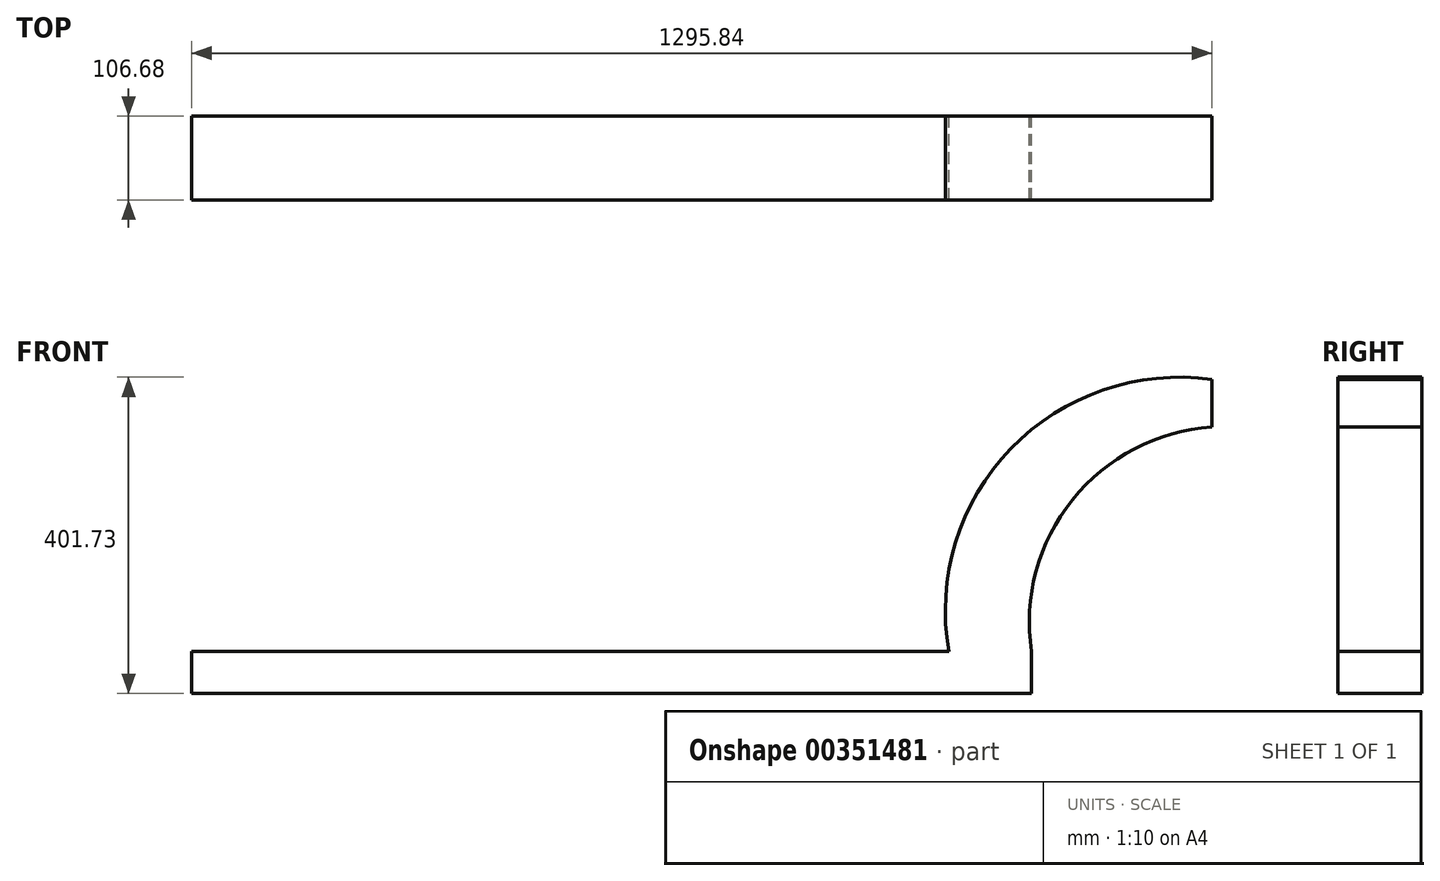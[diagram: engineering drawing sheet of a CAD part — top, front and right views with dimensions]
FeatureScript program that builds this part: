
annotation { "Feature Type Name" : "Feature", "Feature Type Description" : "" }
export const myFeature = defineFeature(function(context is Context, id is Id, definition is map)
    precondition{}
    {
        {
            var Q0;
            Q0=qCreatedBy(makeId("Front.planeOp"),FACE);
            var sketch = newSketch(context, id + "F0", { "sketchPlane" : qUnion([Q0])});
            skLineSegment(sketch, "E0.bottom", {"start": v(-548.92, 0) * mm, "end": v(517.88, 0) * mm});
            skLineSegment(sketch, "E0.top", {"start": v(-548.92, 53.35) * mm, "end": v(412.72, 53.35) * mm});
            skLineSegment(sketch, "E0.left", {"start": v(-548.92, 0) * mm, "end": v(-548.92, 53.35) * mm});
            skLineSegment(sketch, "E0.right", {"start": v(517.88, 0) * mm, "end": v(517.88, 53.35) * mm});
            skArc(sketch, "E1", {"start": v(746.92, 338.17) * mm, "mid": v(569.88, 246.04) * mm, "end": v(517.88, 53.35) * mm});
            skLineSegment(sketch, "E2", {"start": v(746.92, 338.17) * mm, "end": v(746.92, 398.87) * mm});
            skArc(sketch, "E3", {"start": v(746.92, 398.87) * mm, "mid": v(491.96, 311.1) * mm, "end": v(412.72, 53.35) * mm});
            skLineSegment(sketch, "E4", {"start": v(78.3, 53.35) * mm, "end": v(78.3, 142.27) * mm});
            skLineSegment(sketch, "E5", {"start": v(78.3, 142.27) * mm, "end": v(111.33, 142.27) * mm});
            skLineSegment(sketch, "E6", {"start": v(111.33, 142.27) * mm, "end": v(111.33, 53.35) * mm});
            skLineSegment(sketch, "E7", {"start": v(78.3, 97.81) * mm, "end": v(0, 53.35) * mm});
            skLineSegment(sketch, "E8", {"start": v(408.56, 116.39) * mm, "end": v(319.65, 160.06) * mm});
            skLineSegment(sketch, "E9", {"start": v(319.65, 160.06) * mm, "end": v(339.17, 199.8) * mm});
            skLineSegment(sketch, "E10", {"start": v(339.17, 199.8) * mm, "end": v(420.11, 160.06) * mm});
            skSolve(sketch);
        }
        {
            var Q0;
            Q0=makeQuery(id+"F0.imprint","IMPRINT",FACE,{"disambiguationData":[TD([[makeQuery(id+"F0.imprint","IMPRINT",EDGE,{"derivedFrom":sQuery(id+"F0.wireOp",EDGE,"E0.bottom")}),1.0]])]});
            var Q1;
            Q1=sQuery(id+"F0.wireOp",EDGE,"E0.top");
            var Q2;
            Q2=sQuery(id+"F0.wireOp",EDGE,"E0.bottom");
            revolve(context, id + "F1", {"bodyType" : ToolBodyType.SURFACE, "entities" : qUnion([Q0]), "surfaceEntities" : qUnion([Q1]), "axis" : qUnion([Q2]), "revolveType" : RevolveType.FULL});
        }
        {
            var Q0;
            Q0=sQuery(id+"F0.wireOp",EDGE,"E4");
            var Q1;
            Q1=sQuery(id+"F0.wireOp",EDGE,"E6");
            revolve(context, id + "F2", {"bodyType" : ToolBodyType.SURFACE, "surfaceEntities" : qUnion([Q0]), "axis" : qUnion([Q1]), "revolveType" : RevolveType.FULL});
        }
        {
            var Q0;
            Q0=sQuery(id+"F0.wireOp",EDGE,"E8");
            var Q1;
            Q1=sQuery(id+"F0.wireOp",EDGE,"E10");
            revolve(context, id + "F3", {"bodyType" : ToolBodyType.SURFACE, "surfaceEntities" : qUnion([Q0]), "axis" : qUnion([Q1]), "revolveType" : RevolveType.FULL});
        }
        {
            var Q0;
            Q0=makeQuery(id+"F0.imprint","IMPRINT",FACE,{"disambiguationData":[TD([[makeQuery(id+"F0.imprint","IMPRINT",EDGE,{"derivedFrom":sQuery(id+"F0.wireOp",EDGE,"E0.bottom")}),1.0]])]});
            extrude(context, id + "F4", {"entities" : qUnion([Q0]), "endBound" : BoundingType.SYMMETRIC, "depth" : 106.68 * mm});
        }
    });
